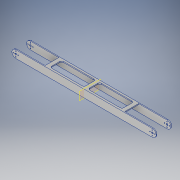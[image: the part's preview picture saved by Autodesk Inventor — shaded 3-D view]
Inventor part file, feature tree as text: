
AUTODESK INVENTOR PART (.ipt)
format: ipt  version: 2017 (Build 210142000, 142)  size: 264,192 bytes
history: native  units: in
note: dims shown in document units (in); Inventor stores cm internally (conversion verified against a paired STEP export)
features: sketch x5, extrude x4, projected_geometry x4, fillet x3, mirror x3, plane x1, hole x1
ambient origin geometry x8: Origin, YZ Plane, XZ Plane, XY Plane, X Axis, Y Axis, Z Axis, Center Point
bodies: Solid1 (feature_tree)
feature tree (21):
  extrude  "Extrusion1"  Depth=1.8105in
  extrude  "Extrusion2"  Depth=0.125in
  fillet  "Fillet1"  Radius=19.0in
  extrude  "Extrusion4"  Depth=0.125in
  fillet  "Fillet2"  Radius=0.125in
  plane  "Work Plane1"
  mirror  "Mirror1"
  fillet  "Fillet3"  Radius=4.25in
  extrude  "Extrusion5"  Depth=0.125in
  mirror  "Mirror2"
  hole  "Hole2"  [1 undecoded]
  mirror  "Mirror3"
  sketch  "Sketch1"  dims[d0=1.0in d2=1.8105in]
  sketch  "Sketch3"  dims[d3=0.875in d4=0.125in d5=19.0in d6=0.0in]
  projected_geometry  "Projected Loop2"
  sketch  "Sketch6"  dims[d14=2.0605in d16=4.25in d17=0.125in d18=0.0in d27=4.25in]
  projected_geometry  "Projected Loop4"
  sketch  "Sketch8"  dims[d28=1.8105in d29=0.125in]
  projected_geometry  "Projected Loop6"
  sketch  "Sketch9"  dims[d30=1.8105in d31=0.125in d32=0.125in d62=0.5in d65=10.5in d66=2.0605in d67=0.25in d68=1.5605in d69=0.5in d70=4.5in d71=1.0in d72=0.0in d73=0.25in d74=0.25in d82=0.1969in d83=0.1137in d84=30.0deg d85=150.0deg d86=30.0deg d87=150.0deg d88=0.0568in d89=0.0984in d90=3.0in d91=0.0in d97=0.6299in d100=0.6299in d101=0.0in d102=0.1969in d103=0.2165in d104=0.2273in d105=0.0in d106=0.2013in d107=0.108in d108=0.75in d109=0.375in d110=0.25in d111=0.5635in d112=2.5in d113=0.8108in]
  projected_geometry  "Projected Loop7"
note: 1 required parameter value undecoded (feature->parameter linkage not recoverable at this tier; creation-order binding heuristic only, values carry confidence <= 0.55)
